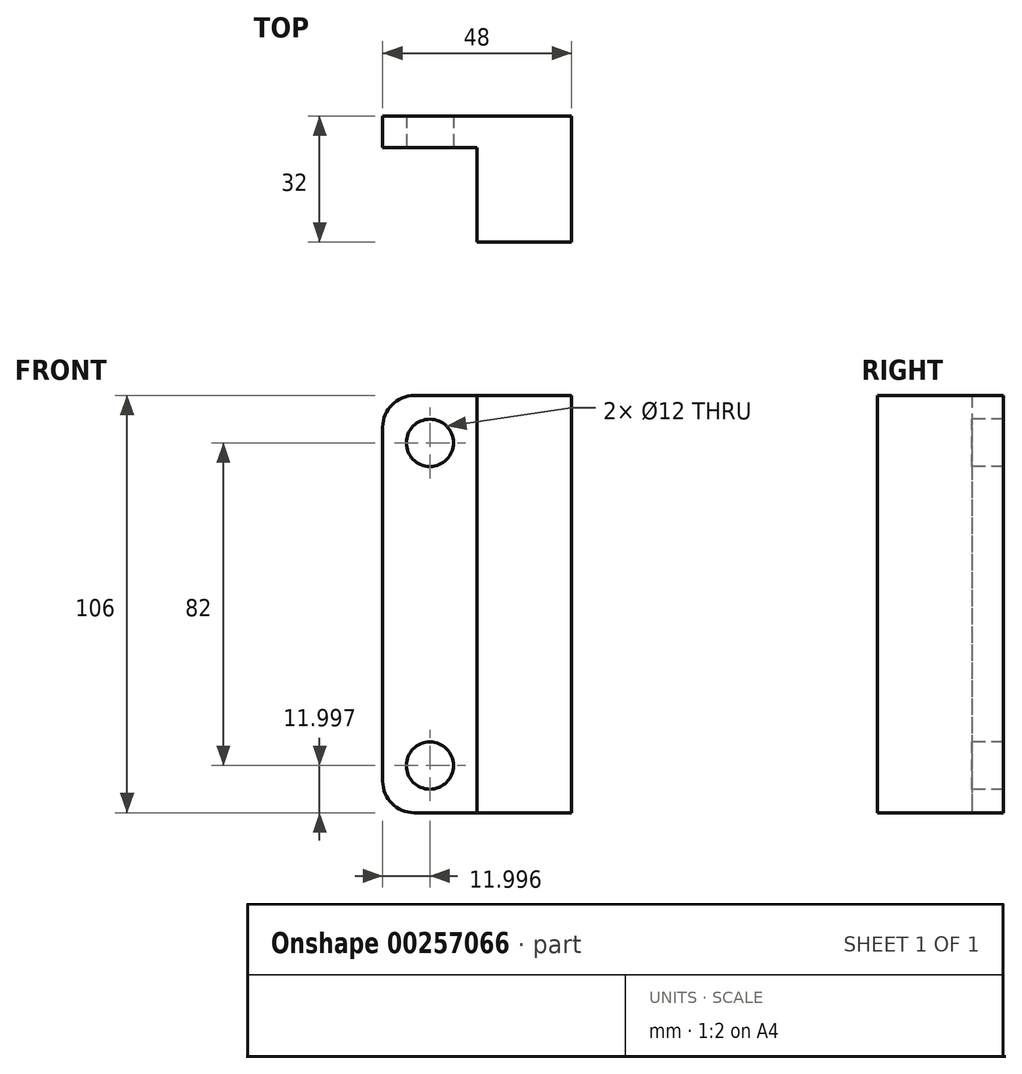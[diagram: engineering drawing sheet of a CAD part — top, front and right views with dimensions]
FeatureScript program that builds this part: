
annotation { "Feature Type Name" : "Feature", "Feature Type Description" : "" }
export const myFeature = defineFeature(function(context is Context, id is Id, definition is map)
    precondition{}
    {
        {
            var Q0;
            Q0=qCreatedBy(makeId("Front.planeOp"),FACE);
            var sketch = newSketch(context, id + "F0", { "sketchPlane" : qUnion([Q0])});
            skLineSegment(sketch, "E0.bottom", {"start": v(-47.98, 54) * mm, "end": v(0.02, 54) * mm});
            skLineSegment(sketch, "E0.top", {"start": v(-47.98, -52) * mm, "end": v(0.02, -52) * mm});
            skLineSegment(sketch, "E0.left", {"start": v(-47.98, 54) * mm, "end": v(-47.98, -52) * mm});
            skLineSegment(sketch, "E0.right", {"start": v(0.02, 54) * mm, "end": v(0.02, -52) * mm});
            skSolve(sketch);
        }
        {
            var Q0;
            Q0 = qSketchRegion(id + "F0", true);
            extrude(context, id + "F1", {"entities" : qUnion([Q0]), "depth" : 8 * mm});
        }
        {
            var Q0;
            Q0=makeQuery(id+"F1.opExtrude","CAP_FACE",FACE,{"disambiguationData":[OSD([sQuery(id+"F0.wireOp",EDGE,"E0.bottom"),sQuery(id+"F0.wireOp",EDGE,"E0.top"),sQuery(id+"F0.wireOp",EDGE,"E0.left"),sQuery(id+"F0.wireOp",EDGE,"E0.right")])],"isStart":false});
            var sketch = newSketch(context, id + "F2", { "sketchPlane" : qUnion([Q0])});
            skLineSegment(sketch, "E1", {"start": v(0.02, 54) * mm, "end": v(-23.98, 54) * mm});
            skLineSegment(sketch, "E2", {"start": v(-23.98, 54) * mm, "end": v(-23.98, -52) * mm});
            skSolve(sketch);
        }
        {
            var Q0;
            Q0=makeQuery(id+"F2.imprint","IMPRINT",FACE,{"disambiguationData":[TD([[makeQuery(id+"F2.imprint","IMPRINT",EDGE,{"derivedFrom":sQuery(id+"F2.wireOp",EDGE,"E1")}),-1.0]])]});
            extrude(context, id + "F3", {"entities" : qUnion([Q0]), "operationType" : NewBodyOperationType.ADD, "depth" : 24 * mm});
        }
        {
            var Q0;
            Q0=makeQuery(id+"F1.opExtrude","CAP_FACE",FACE,{"disambiguationData":[OSD([sQuery(id+"F0.wireOp",EDGE,"E0.bottom"),sQuery(id+"F0.wireOp",EDGE,"E0.top"),sQuery(id+"F0.wireOp",EDGE,"E0.left"),sQuery(id+"F0.wireOp",EDGE,"E0.right")])],"isStart":false});
            var sketch = newSketch(context, id + "F4", { "sketchPlane" : qUnion([Q0])});
            skCircle(sketch, "E3", {"center": v(-35.98, 42) * mm, "radius": 6 * mm});
            skCircle(sketch, "E4", {"center": v(-35.98, -40) * mm, "radius": 6 * mm});
            skSolve(sketch);
        }
        {
            var Q0;
            Q0 = qSketchRegion(id + "F4", true);
            extrude(context, id + "F5", {"entities" : qUnion([Q0]), "operationType" : NewBodyOperationType.REMOVE, "oppositeDirection" : true, "depth" : 40 * mm});
        }
        {
            var Q0;
            Q0=makeQuery(id+"F1.opExtrude","SWEPT_EDGE",EDGE,{"disambiguationData":[OSD([sQuery(id+"F0.wireOp",EDGE,"E0.bottom"),sQuery(id+"F0.wireOp",EDGE,"E0.left")])]});
            var Q1;
            Q1=makeQuery(id+"F1.opExtrude","SWEPT_EDGE",EDGE,{"disambiguationData":[OSD([sQuery(id+"F0.wireOp",EDGE,"E0.top"),sQuery(id+"F0.wireOp",EDGE,"E0.left")])]});
            fillet(context, id + "F6", {"entities" : qUnion([Q0, Q1]), "radius" : 8 * mm, "tangentPropagation" : true, "allowEdgeOverflow" : false});
        }
    });
